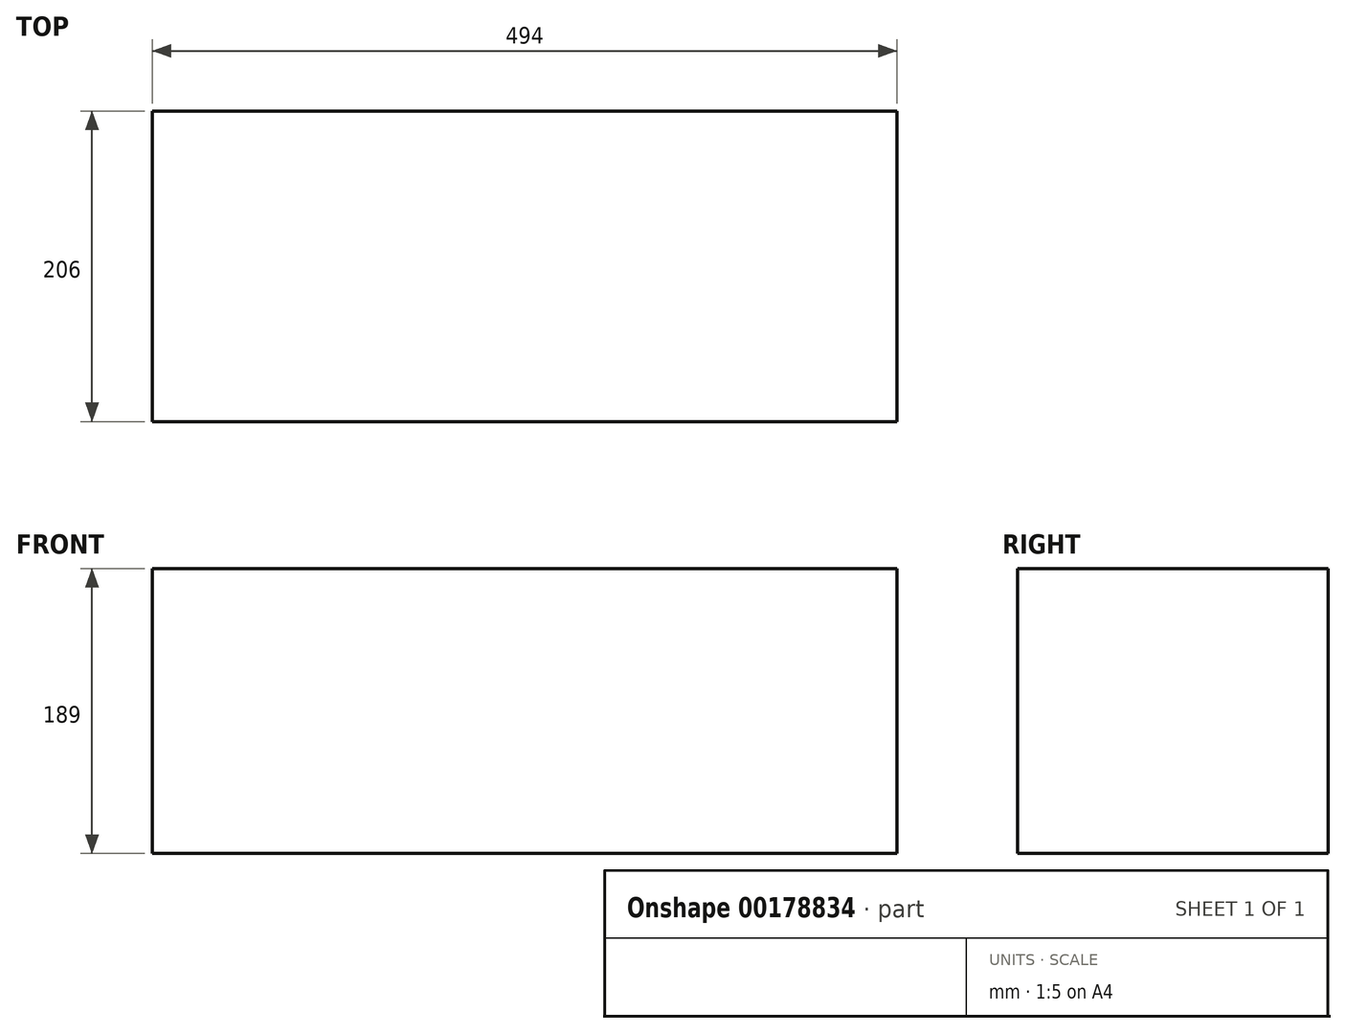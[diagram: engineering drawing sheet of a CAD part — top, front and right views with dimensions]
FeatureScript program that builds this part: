
annotation { "Feature Type Name" : "Feature", "Feature Type Description" : "" }
export const myFeature = defineFeature(function(context is Context, id is Id, definition is map)
    precondition{}
    {
        {
            var Q0;
            Q0=qCreatedBy(makeId("Front.planeOp"),FACE);
            var sketch = newSketch(context, id + "F0", { "sketchPlane" : qUnion([Q0])});
            skLineSegment(sketch, "E0.bottom", {"start": v(-106.05, 203.83) * mm, "end": v(387.95, 203.83) * mm});
            skLineSegment(sketch, "E0.top", {"start": v(-106.05, 14.83) * mm, "end": v(387.95, 14.83) * mm});
            skLineSegment(sketch, "E0.left", {"start": v(-106.05, 203.83) * mm, "end": v(-106.05, 14.83) * mm});
            skLineSegment(sketch, "E0.right", {"start": v(387.95, 203.83) * mm, "end": v(387.95, 14.83) * mm});
            skSolve(sketch);
        }
        {
            var Q0;
            Q0=makeQuery(id+"F0.imprint","IMPRINT",FACE,{"disambiguationData":[TD([[makeQuery(id+"F0.imprint","IMPRINT",EDGE,{"derivedFrom":sQuery(id+"F0.wireOp",EDGE,"E0.bottom")}),-1.0]])]});
            extrude(context, id + "F1", {"entities" : qUnion([Q0]), "oppositeDirection" : true, "offsetDistance" : 25 * mm, "depth" : 206 * mm});
        }
    });
